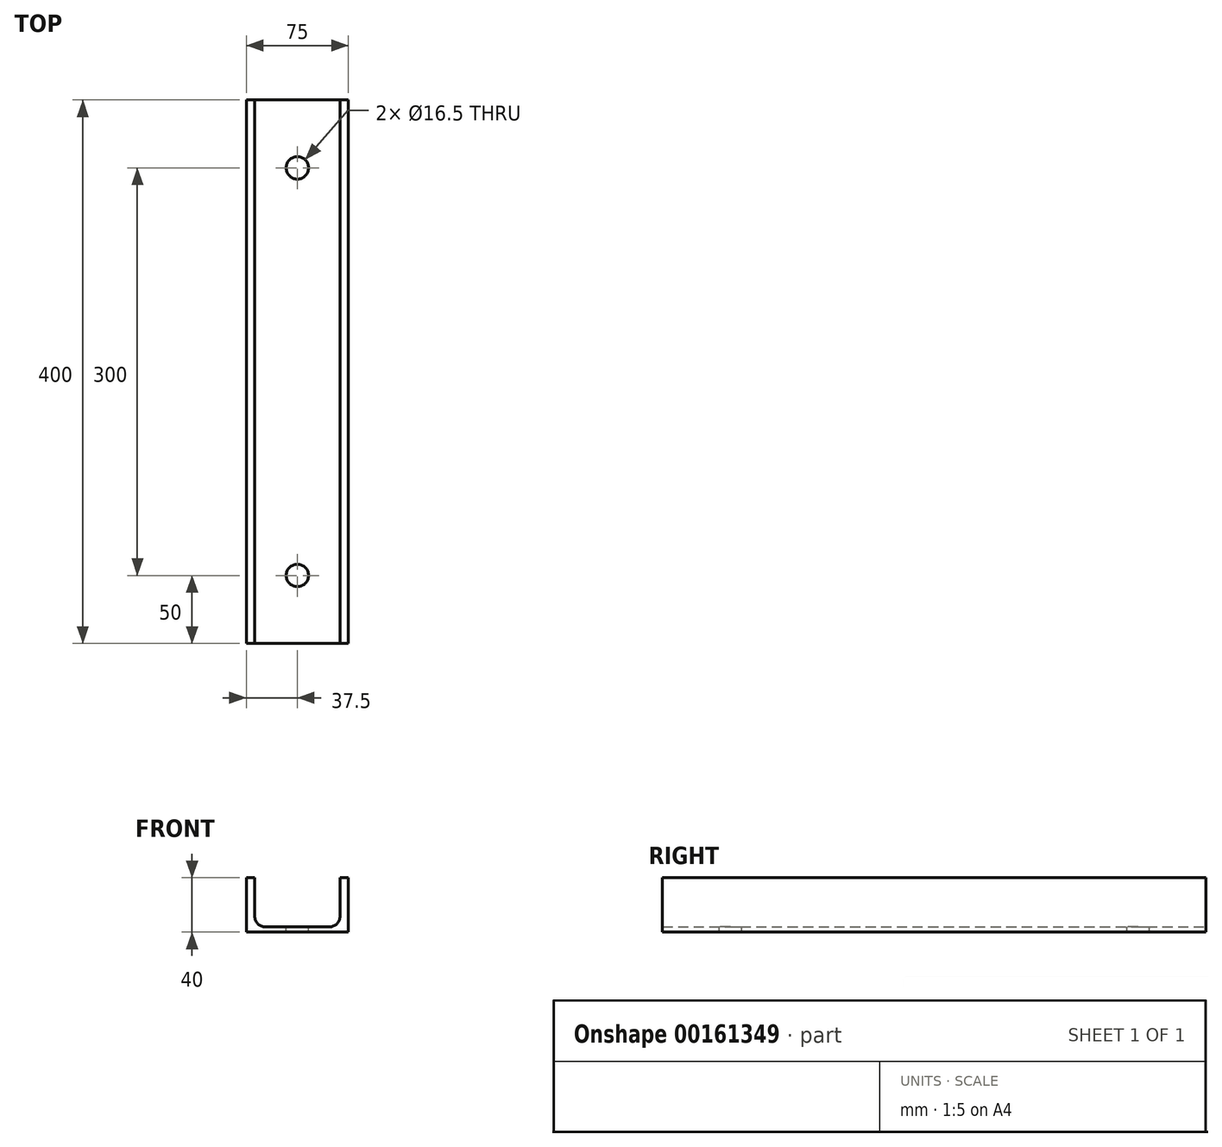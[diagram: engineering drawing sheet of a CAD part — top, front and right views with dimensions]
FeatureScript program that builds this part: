
annotation { "Feature Type Name" : "Feature", "Feature Type Description" : "" }
export const myFeature = defineFeature(function(context is Context, id is Id, definition is map)
    precondition{}
    {
        {
            var Q0;
            Q0=qCreatedBy(makeId("Front.planeOp"),FACE);
            var sketch = newSketch(context, id + "F0", { "sketchPlane" : qUnion([Q0])});
            skLineSegment(sketch, "E0", {"start": v(0, 0) * mm, "end": v(37.5, 0) * mm});
            skLineSegment(sketch, "E1", {"start": v(37.5, 0) * mm, "end": v(37.5, 40) * mm});
            skLineSegment(sketch, "E2", {"start": v(37.5, 40) * mm, "end": v(31.4, 40) * mm});
            skLineSegment(sketch, "E3", {"start": v(31.4, 40) * mm, "end": v(31.4, 11.8) * mm});
            skLineSegment(sketch, "E4", {"start": v(23.4, 3.8) * mm, "end": v(0, 3.8) * mm});
            skLineSegment(sketch, "E5.MirrorCS", {"start": v(-37.5, 40) * mm, "end": v(-31.4, 40) * mm});
            skLineSegment(sketch, "E6.MirrorCS", {"start": v(0, 0) * mm, "end": v(-37.5, 0) * mm});
            skLineSegment(sketch, "E7.MirrorCS", {"start": v(-23.4, 3.8) * mm, "end": v(0, 3.8) * mm});
            skLineSegment(sketch, "E8.MirrorCS", {"start": v(-37.5, 0) * mm, "end": v(-37.5, 40) * mm});
            skLineSegment(sketch, "E9.MirrorCS", {"start": v(-31.4, 40) * mm, "end": v(-31.4, 11.8) * mm});
            skPoint(sketch, "E10.visualSharp", {"position": v(31.4, 3.8) * mm});
            skArc(sketch, "E10.filletArc", {"start": v(23.4, 3.8) * mm, "mid": v(29.06, 6.14) * mm, "end": v(31.4, 11.8) * mm});
            skPoint(sketch, "E11.visualSharp", {"position": v(-31.4, 3.8) * mm});
            skArc(sketch, "E11.filletArc", {"start": v(-31.4, 11.8) * mm, "mid": v(-29.06, 6.14) * mm, "end": v(-23.4, 3.8) * mm});
            skSolve(sketch);
        }
        {
            var Q0;
            Q0=makeQuery(id+"F0.imprint","IMPRINT",FACE,{"disambiguationData":[TD([[makeQuery(id+"F0.imprint","IMPRINT",EDGE,{"derivedFrom":sQuery(id+"F0.wireOp",EDGE,"E0")}),1.0]])]});
            extrude(context, id + "F1", {"entities" : qUnion([Q0]), "depth" : 400 * mm});
        }
        {
            var Q0;
            Q0=qCreatedBy(makeId("Top.planeOp"),FACE);
            var sketch = newSketch(context, id + "F2", { "sketchPlane" : qUnion([Q0])});
            skLineSegment(sketch, "E12", {"start": v(0, 0) * mm, "end": v(0, -447.13) * mm, "construction": true});
            skPoint(sketch, "E13", {"position": v(0, -50) * mm});
            skPoint(sketch, "E14", {"position": v(0, -350) * mm});
            skSolve(sketch);
        }
        {
            var Q0;
            Q0=sQuery(id+"F2.wireOp",VERTEX,"E13");
            var Q1;
            Q1=sQuery(id+"F2.wireOp",VERTEX,"E14");
            var Q2;
            Q2=makeQuery(id+"F1.opExtrude","SWEPT_BODY",BODY,{"disambiguationData":[OSD([sQuery(id+"F0.wireOp",EDGE,"E0"),sQuery(id+"F0.wireOp",EDGE,"E1"),sQuery(id+"F0.wireOp",EDGE,"E2"),sQuery(id+"F0.wireOp",EDGE,"E3"),sQuery(id+"F0.wireOp",EDGE,"E4"),sQuery(id+"F0.wireOp",EDGE,"E5.MirrorCS"),sQuery(id+"F0.wireOp",EDGE,"E6.MirrorCS"),sQuery(id+"F0.wireOp",EDGE,"E7.MirrorCS"),sQuery(id+"F0.wireOp",EDGE,"E8.MirrorCS"),sQuery(id+"F0.wireOp",EDGE,"E9.MirrorCS"),sQuery(id+"F0.wireOp",EDGE,"E10.filletArc"),sQuery(id+"F0.wireOp",EDGE,"E11.filletArc")])]});
            hole(context, id + "F3", {"style" : HoleStyle.SIMPLE, "endStyle" : HoleEndStyle.THROUGH, "oppositeDirection" : true, "standardTappedOrClearance" : lookupTablePath({ "standard" : "ISO", "size" : "16.5", "type" : "Drilled" }), "standardBlindInLast" : lookupTablePath({ "standard" : "ISO", "size" : "16.5", "type" : "Drilled" }), "holeDiameter" : 16.5 * mm, "locations" : qUnion([Q0, Q1]), "scope" : qUnion([Q2]), "isTappedThrough" : true, "startStyle" : HoleStartStyle.PART});
        }
    });
